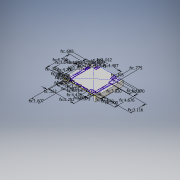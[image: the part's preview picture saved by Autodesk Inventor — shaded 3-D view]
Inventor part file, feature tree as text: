
AUTODESK INVENTOR PART (.ipt)
format: ipt  version: 2017 SP1 (Build 210196100, 196)  size: 189,952 bytes
history: native  units: in
note: dims shown in document units (in); Inventor stores cm internally (conversion verified against a paired STEP export)
features: sketch x3, extrude x1, hole x1, mirror x1
ambient origin geometry x8: Origin, YZ Plane, XZ Plane, XY Plane, X Axis, Y Axis, Z Axis, Center Point
bodies: Solid1 (feature_tree)
feature tree (6):
  extrude  "Extrusion1"  Depth=0.125in
  hole  "Hole1"  [1 undecoded]
  mirror  "Mirror1"
  sketch  "Sketch3"  dims[d4=5.637in d5=0.0in d6=0.1875in d7=1.0in d8=1.0in d9=0.201in d10=0.75in d11=0.385in d12=0.25in d13=0.5635in d14=1.0in d15=0.8108in d16=5.637in d17=5.754in d18=1.24in d19=0.34in d20=1.607in d21=0.051in d22=1.24in d23=0.34in d24=2.907in d25=0.051in d26=0.7in d27=0.865in d28=0.113in d29=4.425in d30=3.04in d31=0.375in d32=0.598in d33=0.162in d34=0.395in d35=0.87in d36=4.407in d37=4.676in d38=0.775in d39=1.42in d40=3.82in d41=0.375in d42=3.116in d43=0.643in d44=5.252in d45=0.445in d46=0.68in d47=1.012in d48=4.796in d49=0.345in d50=0.345in d51=0.707in d52=0.162in d53=0.375in d54=0.375in d55=3.751in d56=0.162in d57=0.42in d58=0.315in d59=0.162in d60=4.2in]
  sketch  "Sketch1"  dims[d0=0.9in d1=0.125in]
  sketch  "Sketch2"  dims[d2=0.375in d3=2.9395in]
note: 1 required parameter value undecoded (feature->parameter linkage not recoverable at this tier; creation-order binding heuristic only, values carry confidence <= 0.55)
